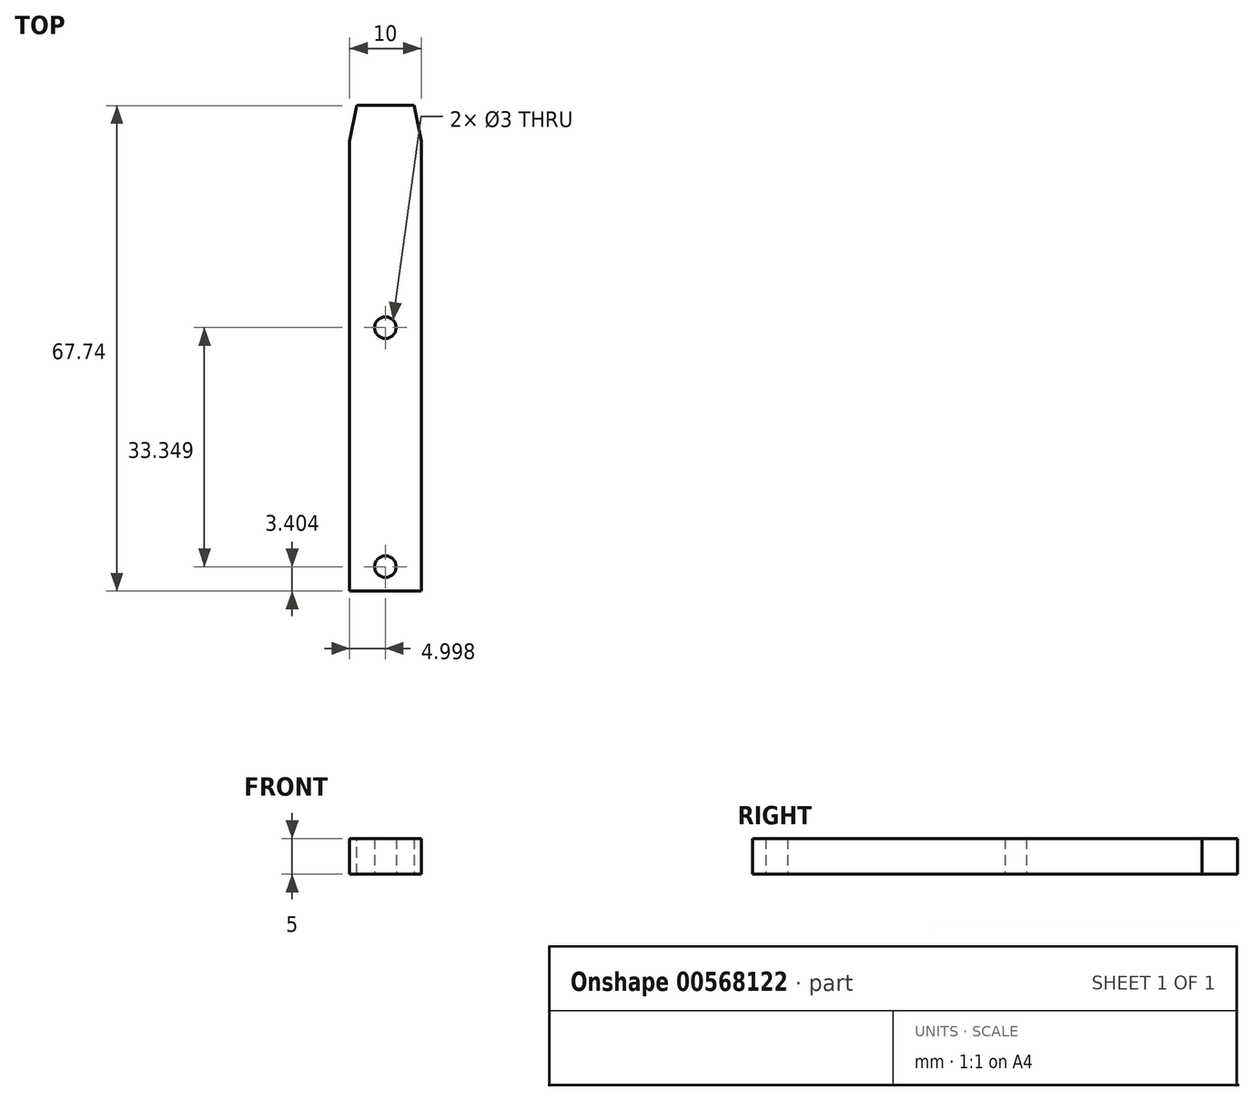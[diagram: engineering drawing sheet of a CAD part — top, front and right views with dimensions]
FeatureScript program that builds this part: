
annotation { "Feature Type Name" : "Feature", "Feature Type Description" : "" }
export const myFeature = defineFeature(function(context is Context, id is Id, definition is map)
    precondition{}
    {
        {
            var Q0;
            Q0=qCreatedBy(makeId("Top.planeOp"),FACE);
            var sketch = newSketch(context, id + "F0", { "sketchPlane" : qUnion([Q0])});
            skLineSegment(sketch, "E0.bottom", {"start": v(-44.61, 45.43) * mm, "end": v(-34.61, 45.43) * mm});
            skLineSegment(sketch, "E0.top", {"start": v(-44.61, -22.3) * mm, "end": v(-34.61, -22.3) * mm});
            skLineSegment(sketch, "E0.left", {"start": v(-44.61, 45.43) * mm, "end": v(-44.61, -22.3) * mm});
            skLineSegment(sketch, "E0.right", {"start": v(-34.61, 45.43) * mm, "end": v(-34.61, -22.3) * mm});
            skCircle(sketch, "E1", {"center": v(-39.61, -18.9) * mm, "radius": 1.5 * mm});
            skCircle(sketch, "E2", {"center": v(-39.61, 14.44) * mm, "radius": 1.5 * mm});
            skPoint(sketch, "E3", {"position": v(-39.61, -22.3) * mm});
            skSolve(sketch);
        }
        {
            var Q0;
            Q0 = qSketchRegion(id + "F0", true);
            extrude(context, id + "F1", {"entities" : qUnion([Q0]), "endBound" : BoundingType.SYMMETRIC, "depth" : 5 * mm, "offsetDistance" : 25 * mm});
        }
        {
            var Q0;
            Q0=makeQuery(id+"F1.opExtrude","SWEPT_EDGE",EDGE,{"disambiguationData":[OSD([sQuery(id+"F0.wireOp",EDGE,"E0.bottom"),sQuery(id+"F0.wireOp",EDGE,"E0.left")])]});
            var Q1;
            Q1=makeQuery(id+"F1.opExtrude","SWEPT_EDGE",EDGE,{"disambiguationData":[OSD([sQuery(id+"F0.wireOp",EDGE,"E0.bottom"),sQuery(id+"F0.wireOp",EDGE,"E0.right")])]});
            chamfer(context, id + "F2", {"entities" : qUnion([Q0, Q1]), "chamferType" : ChamferType.TWO_OFFSETS, "width1" : 5 * mm, "oppositeDirection" : false, "width2" : 1 * mm, "tangentPropagation" : true});
        }
    });
